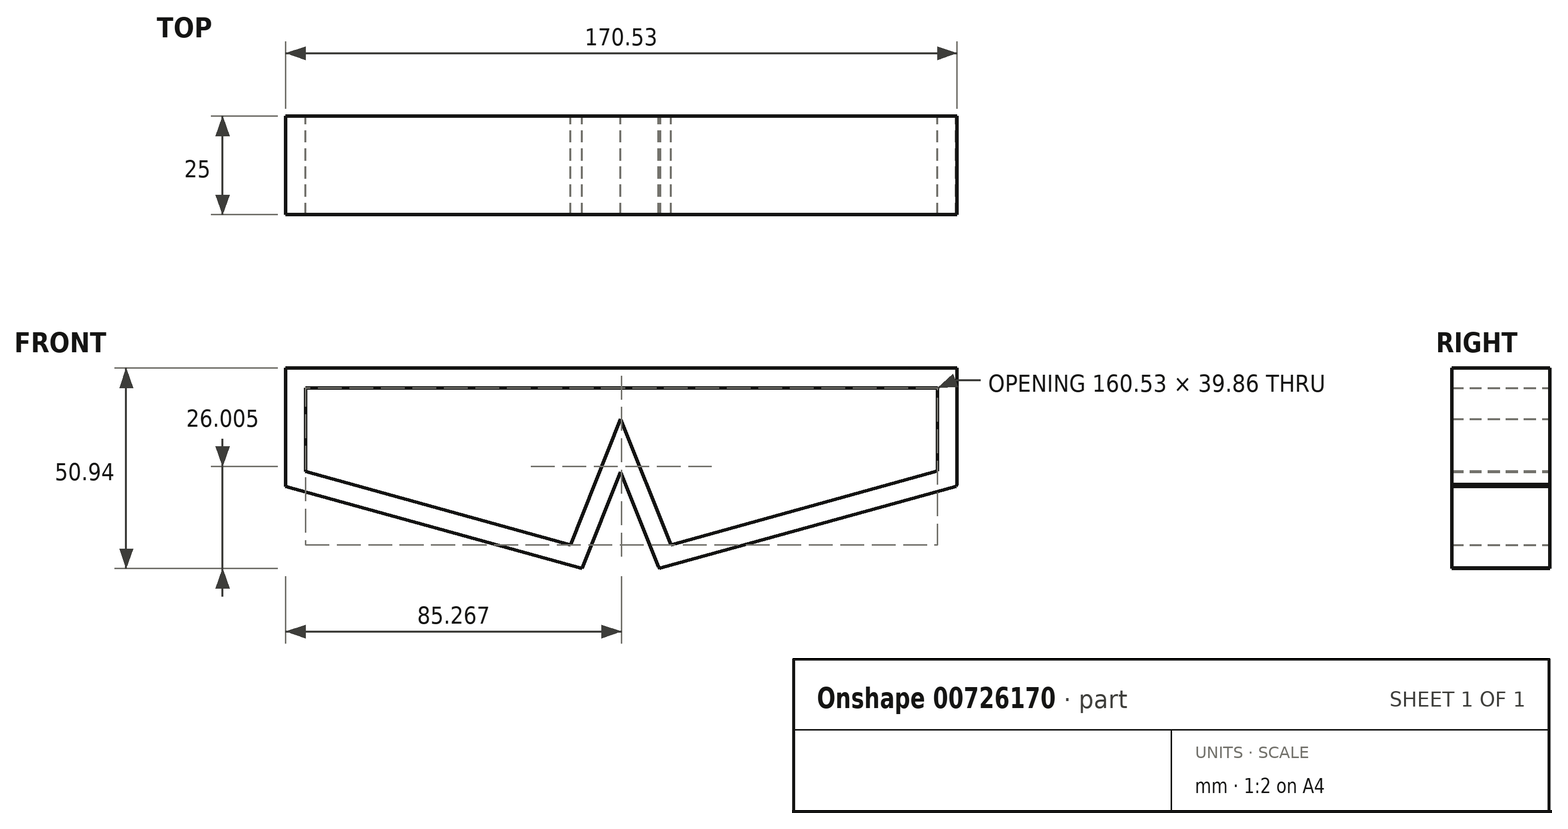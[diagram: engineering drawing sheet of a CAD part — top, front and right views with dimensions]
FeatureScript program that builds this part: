
annotation { "Feature Type Name" : "Feature", "Feature Type Description" : "" }
export const myFeature = defineFeature(function(context is Context, id is Id, definition is map)
    precondition{}
    {
        {
            var Q0;
            Q0=qCreatedBy(makeId("Front.planeOp"),FACE);
            var sketch = newSketch(context, id + "F0", { "sketchPlane" : qUnion([Q0])});
            skLineSegment(sketch, "E0.top", {"start": v(-6.28, 52.27) * mm, "end": v(-91.28, 52.27) * mm});
            skLineSegment(sketch, "E0.right", {"start": v(-91.28, 22.27) * mm, "end": v(-91.28, 52.27) * mm});
            skPoint(sketch, "E1.oppositeSnap0", {"position": v(-48.78, 52.27) * mm});
            skLineSegment(sketch, "E1.bottom", {"start": v(-48.78, 52.27) * mm, "end": v(-46.59, 52.27) * mm});
            skLineSegment(sketch, "E1.top", {"start": v(-48.78, 41.07) * mm, "end": v(-48.43, 41.07) * mm});
            skLineSegment(sketch, "E2", {"start": v(-15.96, 1.39) * mm, "end": v(-6.17, 25.85) * mm});
            skLineSegment(sketch, "E3", {"start": v(-15.96, 1.39) * mm, "end": v(-91.28, 22.27) * mm});
            skLineSegment(sketch, "E4.MirrorCS", {"start": v(-6.28, 52.27) * mm, "end": v(78.72, 52.27) * mm});
            skLineSegment(sketch, "E5.MirrorCS", {"start": v(79.25, 22.67) * mm, "end": v(79.25, 52.27) * mm});
            skLineSegment(sketch, "E6.MirrorCS", {"start": v(3.99, 1.49) * mm, "end": v(78.95, 22.27) * mm});
            skLineSegment(sketch, "E7.MirrorCS", {"start": v(3.49, 1.74) * mm, "end": v(-6.17, 25.85) * mm});
            skLineSegment(sketch, "E8.0", {"start": v(6.6, 7.4) * mm, "end": v(-1.92, 28.69) * mm});
            skLineSegment(sketch, "E9.0", {"start": v(-18.94, 7.4) * mm, "end": v(-10.42, 28.69) * mm});
            skLineSegment(sketch, "E10.0", {"start": v(-18.94, 7.4) * mm, "end": v(-6.17, 39.3) * mm});
            skLineSegment(sketch, "E10.1", {"start": v(6.6, 7.4) * mm, "end": v(-6.17, 39.3) * mm});
            skLineSegment(sketch, "E10.2", {"start": v(-18.94, 7.4) * mm, "end": v(-86.28, 26.07) * mm});
            skLineSegment(sketch, "E10.3", {"start": v(6.6, 7.4) * mm, "end": v(74.25, 26.15) * mm});
            skLineSegment(sketch, "E10.4", {"start": v(-86.28, 26.07) * mm, "end": v(-86.28, 47.27) * mm});
            skLineSegment(sketch, "E10.5", {"start": v(-6.28, 47.27) * mm, "end": v(-86.28, 47.27) * mm});
            skLineSegment(sketch, "E10.6", {"start": v(-6.28, 47.27) * mm, "end": v(74.25, 47.27) * mm});
            skLineSegment(sketch, "E10.7", {"start": v(74.25, 26.15) * mm, "end": v(74.25, 47.27) * mm});
            skLineSegment(sketch, "E11", {"start": v(3.49, 1.74) * mm, "end": v(3.69, 1.33) * mm});
            skLineSegment(sketch, "E12", {"start": v(3.69, 1.33) * mm, "end": v(3.99, 1.49) * mm});
            skLineSegment(sketch, "E13", {"start": v(78.72, 52.27) * mm, "end": v(79.25, 52.27) * mm});
            skLineSegment(sketch, "E14", {"start": v(78.95, 22.27) * mm, "end": v(79.25, 22.67) * mm});
            skSolve(sketch);
        }
        {
            var Q0;
            {var subQ8=sQuery(id+"F0.wireOp",EDGE,"E0.right");Q0=makeQuery(id+"F0.imprint","IMPRINT",FACE,{"disambiguationData":[TD([[makeQuery(id+"F0.imprint","IMPRINT",EDGE,{"derivedFrom":subQ8}),-1.0]])]});}
            extrude(context, id + "F1", {"entities" : qUnion([Q0]), "depth" : 25 * mm, "offsetDistance" : 25 * mm});
        }
    });
